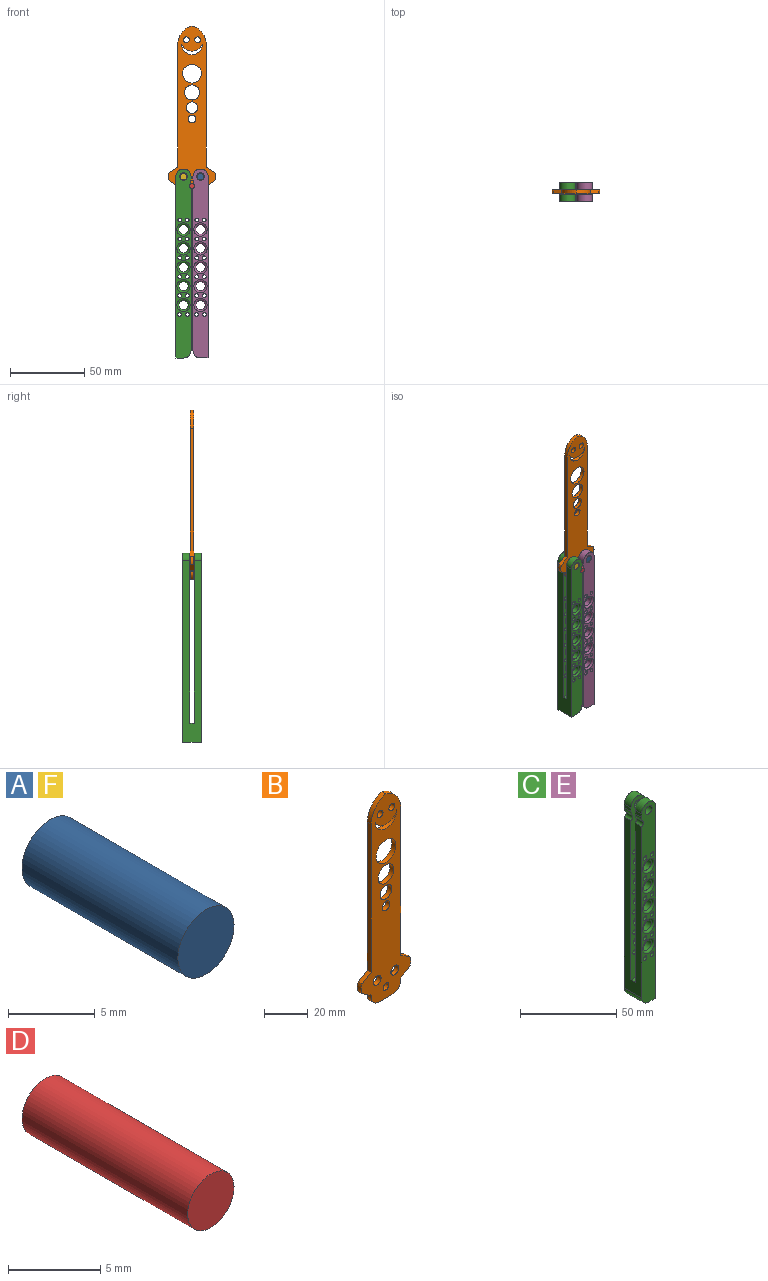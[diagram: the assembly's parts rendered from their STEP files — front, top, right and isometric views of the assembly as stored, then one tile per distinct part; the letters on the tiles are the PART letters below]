
ASSEMBLY  parts=6 mates=5
PART A: 3 faces, bbox 4.6x12.7x4.6 mm
  f0: cylinder r=2.29mm len=12.7mm, axis (0,-1,0), area 182.4mm2, adj f1,f2
  f1: plane 4.57x4.57mm, normal (0,1,0), area 16.4mm2, adj f0
  f2: plane 4.57x4.57mm, normal (0,-1,0), area 16.4mm2, adj f0
PART B: 28 faces, bbox 31.8x2.5x113.9 mm
  f0: plane 2.54x1.27mm, normal (1,0,0), area 3.2mm2, adj f4,f5,f12,f25
  f1: plane 82.55x2.54mm, normal (-1,0,0), area 209.7mm2, adj f4,f5,f6,f22
  f2: plane 82.55x2.54mm, normal (1,0,0), area 209.7mm2, adj f4,f5,f7,f27
  f3: plane 2.54x1.27mm, normal (-1,0,0), area 3.2mm2, adj f4,f5,f11,f24
  f4: plane 113.9x31.75mm, normal (0,1,0), area 1828.1mm2, adj f0,f1,f2,f3,f6,f7,f8,f9
  f5: plane 113.9x31.75mm, normal (0,-1,0), area 1828.1mm2, adj f0,f1,f2,f3,f6,f7,f8,f9
  f6: cylinder r=12.7mm len=12.3mm, axis (0,1,0), area 42.5mm2, adj f1,f4,f5,f7
  f7: cylinder r=12.7mm len=12.3mm, axis (0,-1,0), area 42.5mm2, adj f2,f4,f5,f6
  f8: plane 8.89x2.54mm, normal (0,0,-1), area 22.6mm2, adj f4,f5,f11,f12
  f9: cylinder r=2.54mm len=5.08mm, axis (0,-1,0), area 40.5mm2, adj f4,f5
  f10: cylinder r=2.54mm len=5.08mm, axis (0,-1,0), area 40.5mm2, adj f4,f5
  f11: cylinder r=5.08mm len=5.08mm, axis (0,-1,0), area 20.3mm2, adj f3,f4,f5,f8
  f12: cylinder r=5.08mm len=5.08mm, axis (0,1,0), area 20.3mm2, adj f0,f4,f5,f8
  f13: cylinder r=1.91mm len=3.81mm, axis (0,-1,0), area 30.4mm2, adj f4,f5
  f14: cylinder r=1.91mm len=3.81mm, axis (0,-1,0), area 30.4mm2, adj f4,f5
  f15: cylinder r=1.91mm len=3.81mm, axis (0,-1,0), area 30.4mm2, adj f4,f5
  f16: cylinder r=6.99mm len=13.97mm, axis (0,-1,0), area 55.7mm2, adj f4,f5,f17
  f17: cylinder r=7.62mm len=13.97mm, axis (0,-1,0), area 44.9mm2, adj f4,f5,f16
  f18: cylinder r=6.35mm len=12.7mm, axis (0,-1,0), area 101.3mm2, adj f4,f5
  f19: cylinder r=5.08mm len=10.16mm, axis (0,-1,0), area 81.1mm2, adj f4,f5
  f20: cylinder r=3.81mm len=7.62mm, axis (0,-1,0), area 60.8mm2, adj f4,f5
  f21: cylinder r=2.54mm len=5.08mm, axis (0,-1,0), area 40.5mm2, adj f4,f5
  f22: plane 5.71x3.57mm, normal (-0.53,0,0.85), area 17.1mm2, adj f1,f4,f5,f23
  f23: cylinder r=6.35mm len=5.57mm, axis (0,-1,0), area 14.6mm2, adj f4,f5,f22,f24
  f24: plane 5.71x3.57mm, normal (-0.53,0,-0.85), area 17.1mm2, adj f3,f4,f5,f23
  f25: plane 5.71x3.57mm, normal (0.53,0,-0.85), area 17.1mm2, adj f0,f4,f5,f26
  f26: cylinder r=6.35mm len=5.57mm, axis (0,-1,0), area 14.6mm2, adj f4,f5,f25,f27
  f27: plane 5.71x3.57mm, normal (0.53,0,0.85), area 17.1mm2, adj f2,f4,f5,f26
PART C: 63 faces, bbox 11.6x12.7x127 mm
  f0: plane 108.69x12.7mm, normal (-1,0,0), area 1072.3mm2, adj f6,f7,f9,f10,f11,f14,f15,f16
  f1: plane 4.83x2.33mm, normal (-1,0,0), area 11.3mm2, adj f6,f9,f13,f18
  f2: plane 121.92x12.7mm, normal (1,0,0), area 1215.5mm2, adj f5,f6,f7,f9,f10,f11,f12,f13
  f3: cylinder r=2.54mm len=5.08mm, axis (0,-1,0), area 77mm2, adj f7,f10
  f4: plane 4.83x2.33mm, normal (-1,0,0), area 11.3mm2, adj f7,f10,f12,f17
  f5: plane 12.7x5.08mm, normal (0,0,-1), area 64.5mm2, adj f2,f6,f7,f14
  f6: plane 127x10.16mm, normal (0,1,0), area 878.5mm2, adj f0,f1,f2,f5,f8,f13,f14,f16
  f7: plane 127x10.16mm, normal (0,-1,0), area 878.5mm2, adj f0,f2,f3,f4,f5,f12,f14,f15
  f8: cylinder r=2.54mm len=5.08mm, axis (0,-1,0), area 77mm2, adj f6,f9
  f9: plane 114.3x10.16mm, normal (0,-1,0), area 907mm2, adj f0,f1,f2,f8,f11,f13,f16,f18
  f10: plane 114.3x10.16mm, normal (0,1,0), area 907mm2, adj f0,f2,f3,f4,f11,f12,f15,f17
  f11: plane 10.16x3.05mm, normal (0,0,1), area 31mm2, adj f0,f2,f9,f10
  f12: cylinder r=5.08mm len=10.16mm, axis (0,1,0), area 77mm2, adj f2,f4,f7,f10
  f13: cylinder r=5.08mm len=10.16mm, axis (0,-1,0), area 77mm2, adj f1,f2,f6,f9
  f14: cylinder r=5.08mm len=12.7mm, axis (0,1,0), area 101.3mm2, adj f0,f5,f6,f7
  f15: cylinder r=1.91mm len=4.83mm, axis (0,-1,0), area 16.9mm2, adj f0,f7,f10,f17
  f16: cylinder r=1.91mm len=4.83mm, axis (0,-1,0), area 16.9mm2, adj f0,f6,f9,f18
  f17: cylinder r=5.08mm len=4.83mm, axis (0,-1,0), area 15mm2, adj f4,f7,f10,f15
  f18: cylinder r=5.08mm len=4.83mm, axis (0,-1,0), area 15mm2, adj f1,f6,f9,f16
  f19: cylinder r=1.27mm len=4.83mm, axis (0,-1,0), area 38.5mm2, adj f7,f10
  f20: cylinder r=1.27mm len=4.83mm, axis (0,-1,0), area 38.5mm2, adj f7,f10
  f21: cylinder r=3.17mm len=6.35mm, axis (0,-1,0), area 70.9mm2, adj f10,f62
  f22: cylinder r=1.27mm len=4.83mm, axis (0,-1,0), area 38.5mm2, adj f7,f10
  f23: cylinder r=1.27mm len=4.83mm, axis (0,-1,0), area 38.5mm2, adj f7,f10
  f24: cylinder r=3.17mm len=6.35mm, axis (0,-1,0), area 70.9mm2, adj f10,f60
  f25: cylinder r=1.27mm len=4.83mm, axis (0,-1,0), area 38.5mm2, adj f7,f10
  f26: cylinder r=1.27mm len=4.83mm, axis (0,-1,0), area 38.5mm2, adj f7,f10
  f27: cylinder r=3.17mm len=6.35mm, axis (0,-1,0), area 70.9mm2, adj f10,f61
  f28: cylinder r=1.27mm len=4.83mm, axis (0,-1,0), area 38.5mm2, adj f7,f10
  f29: cylinder r=1.27mm len=4.83mm, axis (0,-1,0), area 38.5mm2, adj f7,f10
  f30: cylinder r=3.17mm len=6.35mm, axis (0,-1,0), area 70.9mm2, adj f10,f58
  f31: cylinder r=1.27mm len=4.83mm, axis (0,-1,0), area 38.5mm2, adj f7,f10
  f32: cylinder r=1.27mm len=4.83mm, axis (0,-1,0), area 38.5mm2, adj f7,f10
  f33: cylinder r=3.17mm len=6.35mm, axis (0,-1,0), area 70.9mm2, adj f10,f59
  f34: cylinder r=1.27mm len=4.83mm, axis (0,-1,0), area 38.5mm2, adj f7,f10
  f35: cylinder r=1.27mm len=4.83mm, axis (0,-1,0), area 38.5mm2, adj f7,f10
  f36: cylinder r=1.27mm len=4.83mm, axis (0,-1,0), area 38.5mm2, adj f6,f9
  f37: cylinder r=1.27mm len=4.83mm, axis (0,-1,0), area 38.5mm2, adj f6,f9
  f38: cylinder r=3.17mm len=6.35mm, axis (0,-1,0), area 70.9mm2, adj f9,f57
  f39: cylinder r=1.27mm len=4.83mm, axis (0,-1,0), area 38.5mm2, adj f6,f9
  f40: cylinder r=1.27mm len=4.83mm, axis (0,-1,0), area 38.5mm2, adj f6,f9
  f41: cylinder r=3.17mm len=6.35mm, axis (0,-1,0), area 70.9mm2, adj f9,f56
  f42: cylinder r=1.27mm len=4.83mm, axis (0,-1,0), area 38.5mm2, adj f6,f9
  f43: cylinder r=1.27mm len=4.83mm, axis (0,-1,0), area 38.5mm2, adj f6,f9
  f44: cylinder r=3.17mm len=6.35mm, axis (0,-1,0), area 70.9mm2, adj f9,f55
  f45: cylinder r=1.27mm len=4.83mm, axis (0,-1,0), area 38.5mm2, adj f6,f9
  f46: cylinder r=1.27mm len=4.83mm, axis (0,-1,0), area 38.5mm2, adj f6,f9
  f47: cylinder r=3.17mm len=6.35mm, axis (0,-1,0), area 70.9mm2, adj f9,f54
  f48: cylinder r=1.27mm len=4.83mm, axis (0,-1,0), area 38.5mm2, adj f6,f9
  f49: cylinder r=1.27mm len=4.83mm, axis (0,-1,0), area 38.5mm2, adj f6,f9
  f50: cylinder r=3.17mm len=6.35mm, axis (0,-1,0), area 70.9mm2, adj f9,f53
  f51: cylinder r=1.27mm len=4.83mm, axis (0,-1,0), area 38.5mm2, adj f6,f9
  f52: cylinder r=1.27mm len=4.83mm, axis (0,-1,0), area 38.5mm2, adj f6,f9
  f53: torus R=4.45mm, axis (0,-1,0), area 45.6mm2, adj f6,f50
  f54: torus R=4.45mm, axis (0,-1,0), area 45.6mm2, adj f6,f47
  f55: torus R=4.45mm, axis (0,-1,0), area 45.6mm2, adj f6,f44
  f56: torus R=4.45mm, axis (0,-1,0), area 45.6mm2, adj f6,f41
  f57: torus R=4.45mm, axis (0,-1,0), area 45.6mm2, adj f6,f38
  f58: torus R=4.45mm, axis (0,-1,0), area 45.6mm2, adj f7,f30
  f59: torus R=4.45mm, axis (0,-1,0), area 45.6mm2, adj f7,f33
  f60: torus R=4.45mm, axis (0,-1,0), area 45.6mm2, adj f7,f24
  f61: torus R=4.45mm, axis (0,-1,0), area 45.6mm2, adj f7,f27
  f62: torus R=4.45mm, axis (0,-1,0), area 45.6mm2, adj f7,f21
PART D: 3 faces, bbox 3.6x12.7x3.6 mm
  f0: cylinder r=1.78mm len=12.7mm, axis (0,-1,0), area 141.9mm2, adj f1,f2
  f1: plane 3.56x3.56mm, normal (0,1,0), area 9.9mm2, adj f0
  f2: plane 3.56x3.56mm, normal (0,-1,0), area 9.9mm2, adj f0
PART E: same geometry as C
PART F: same geometry as A
PLACE A t=(-60.8,-11.46,5.69)mm
PLACE B t=(-56.99,-6.38,5.69)mm fixed
PLACE C rot(axis=(0,0,-1),180deg) t=(-67.15,1.24,-116.23)mm
PLACE D t=(-66.52,-11.46,-0.66)mm
PLACE E rot(axis=(0,-1,0),0deg) t=(-65.88,-11.46,-116.23)mm
PLACE F t=(-72.23,-11.46,5.69)mm
MATE fastened D.f0 <-> B.f13  axis (0,-1,0) through (-66.52,-5.11,-0.66)mm
MATE revolute E.f3 <-> A.f0  axis (0,-1,0) through (-60.8,-11.46,5.69)mm
MATE fastened F.f0 <-> B.f9  axis (0,-1,0) through (-72.23,-5.11,5.69)mm
MATE fastened A.f0 <-> B.f10  axis (0,-1,0) through (-60.8,-5.11,5.69)mm
MATE revolute C.f3 <-> F.f0  axis (0,-1,0) through (-72.23,-11.46,5.69)mm
